# Revit family: ALD UNI LED
name_source: partatom
category: Осветительные приборы
revit_build: Autodesk Revit 2016 (Build: 20150220_1215(x64)
units: mm (PartAtom-declared; Revit-internal decimal feet)

## family parameters
Источник света = Да
Общий = Нет
Основа = Грань
При загрузке вырезать с полостями = Нет
Размер круглого соединителя = Использовать диаметр
Тип детали = Нормальный
Точка расчета площади = Нет

## types (7) — shared parameters
ADSK_Единица измерения = Шт.
ADSK_Завод-изготовитель = ООО МГК Световые технологии
ADSK_Код изделия = 1050000090
ADSK_Количество фаз = 1
ADSK_Количество фаз числовое = 1
ADSK_Наименование = Высокоэффективные светодиодные светильники, совместимые с самыми популярными типами реечных потолков. Могут применяться как внутри здания, так и снаружи под навесом (IP54).
ADSK_Напряжение = 230 В
ADSK_Номинальная мощность = 0 кВт
ADSK_Полная мощность = 0 кВ·А
ADSK_Ток = 0 А
B = 240 мм
E = 142 мм
IP Class = IP54
URL = https://ltcompany.com
Видимая форма излучения при визуализации = Нет
Группа модели = Светильники
Изготовитель = ООО МГК Световые технологии
Излучение по длине прямоугольника = 142 мм
Класс Защиты = I
Класс пожароопасности = П-II,IIа
Код по классификатору = D5020200
Корпус = Белый металл
Область использования = Гостиницы, Индивидуальные дома, Культурно-развлекательные, Магазины/Бутики ,Объекты бытового обслуживания, Объекты общественного питания, Офисы, ТРЦ
Описание = Высокоэффективные светодиодные светильники, совместимые с самыми популярными типами реечных потолков. Могут применяться как внутри здания, так и снаружи под навесом (IP54).
Плафон = Плафон самосвечение
Полная установленная мощность = 0 кВ·А
Разработчик = ООО ПРОРУБИМ
Разработчик (телефон) = +7 (495) 649-85-43
Светофильтр = 16777215
Смещение цветовой температуры при затухании лампы = <Нет>
Тип ИС = LED
Тип продукции = Cветильник
Угол наклона = -90.00°
zero-valued in all types: Отметка по умолчанию

## per-type parameters (varying)
| type | A | ADSK_Коэффициент мощности | ADSK_Масса | ADSK_Энергоэффективность | D | Блок аварийного питания | Излучение по ширине прямоугольника | Климатическая зона | Тип ПРА | Файл фотометрической сетки |
| ALD UNI LED 1200 4000K | 1289 мм | 0.96 | 5.1 | 100 лм/Вт | 1250 мм | Нет | 1250 мм | УХЛ2 | Драйвер | ALD UNI LED 1200 4000K.ies |
| ALD UNI LED 1200 EM 4000K | 1289 мм | 0.9 | 5.1 | 100 лм/Вт | 1250 мм | Да | 1250 мм | УХЛ4 | Драйвер | ALD UNI LED 1200 4000K.ies |
| ALD UNI LED 600 4000K | 680 мм | 0.96 | 4.1 | 92 лм/Вт | 640 мм | Нет | 640 мм | УХЛ2 | Драйвер | ALD UNI LED 600 4000K.ies |
| ALD UNI LED 600 EM 4000K | 680 мм | 0.9 | 4.1 | 92 лм/Вт | 640 мм | Да | 640 мм | УХЛ4 | Драйвер | ALD UNI LED 600 4000K.ies |
| ALD UNI LED 600 HFD 4000K | 680 мм | 0.96 | 4.1 | 92 лм/Вт | 640 мм | Нет | 640 мм | УХЛ2 | Драйвер DALI | ALD UNI LED 600 4000K.ies |
| ALD UNI LED 600 HFD EM 4000K | 680 мм | 0.96 | 4.1 | 92 лм/Вт | 640 мм | Да | 640 мм | УХЛ4 | Драйвер DALI | ALD UNI LED 600 4000K.ies |
| ALD UNI LED 600 3000K | 680 мм | 0.96 | 4.1 | 92 лм/Вт | 640 мм | Нет | 640 мм | УХЛ2 | Драйвер | ALD UNI LED 600 4000K.ies |
